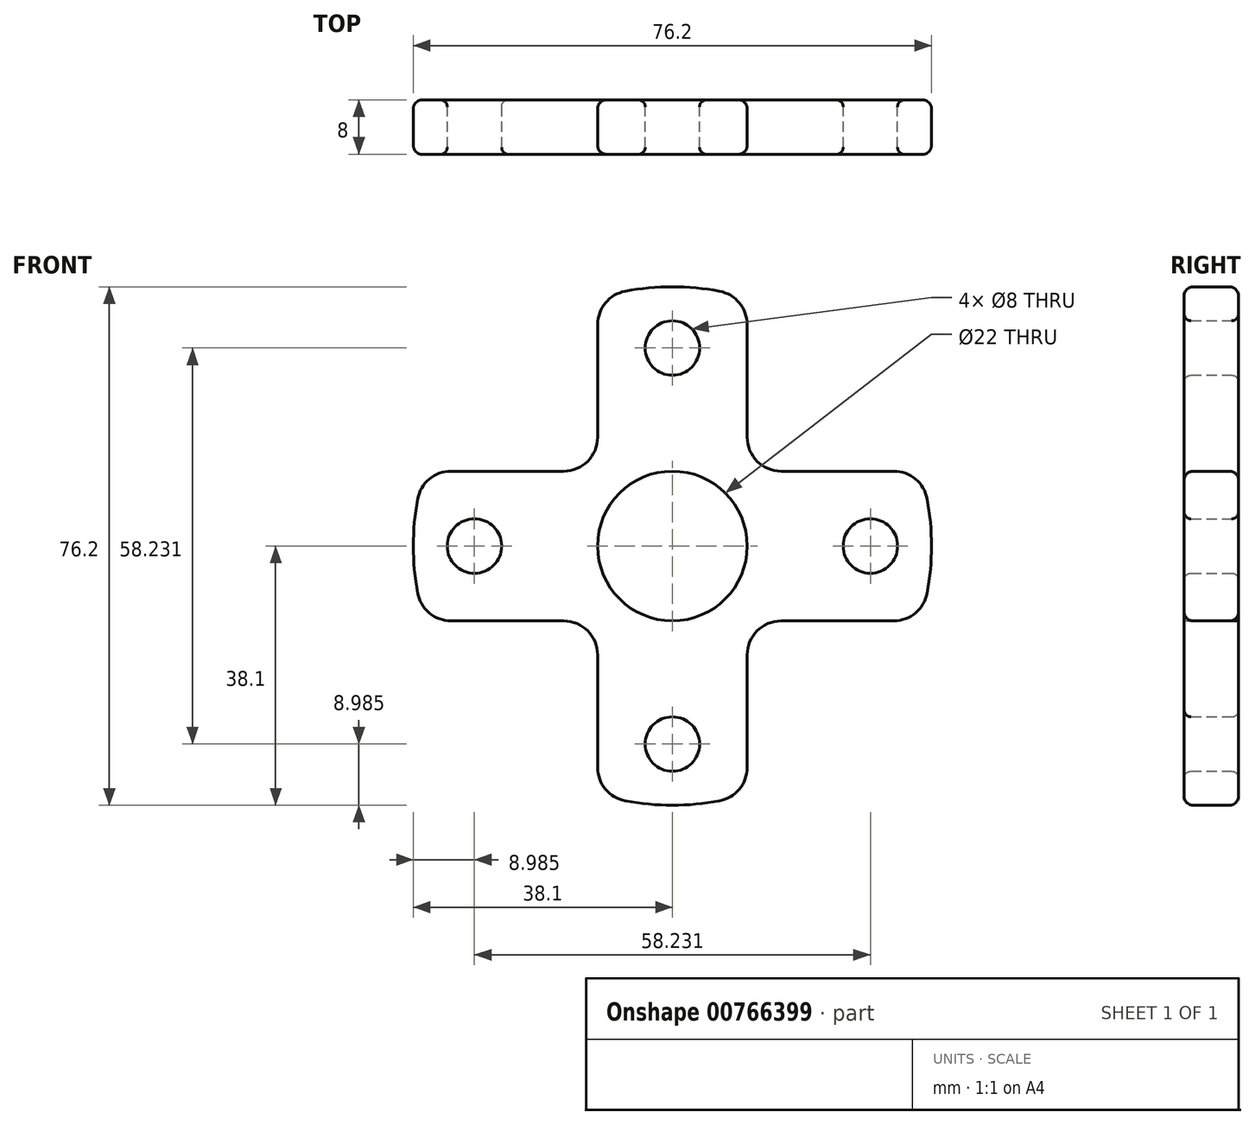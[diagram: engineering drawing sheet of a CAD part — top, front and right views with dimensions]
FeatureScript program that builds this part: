
annotation { "Feature Type Name" : "Feature", "Feature Type Description" : "" }
export const myFeature = defineFeature(function(context is Context, id is Id, definition is map)
    precondition{}
    {
        {
            var Q0;
            Q0=qCreatedBy(makeId("Front.planeOp"),FACE);
            var sketch = newSketch(context, id + "F0", { "sketchPlane" : qUnion([Q0])});
            skArc(sketch, "E0", {"start": v(-37.47, 6.9) * mm, "mid": v(-38.1, 0) * mm, "end": v(-37.47, -6.9) * mm});
            skCircle(sketch, "E1", {"center": v(0, 0) * mm, "radius": 11 * mm});
            skLineSegment(sketch, "E2", {"start": v(16, 11) * mm, "end": v(32.55, 11) * mm});
            skLineSegment(sketch, "E3", {"start": v(16, -11) * mm, "end": v(32.55, -11) * mm});
            skLineSegment(sketch, "E4", {"start": v(-16, -11) * mm, "end": v(-32.55, -11) * mm});
            skLineSegment(sketch, "E5", {"start": v(-16, 11) * mm, "end": v(-32.55, 11) * mm});
            skLineSegment(sketch, "E6", {"start": v(11, -16) * mm, "end": v(11, -32.55) * mm});
            skLineSegment(sketch, "E7", {"start": v(-11, -16) * mm, "end": v(-11, -32.55) * mm});
            skLineSegment(sketch, "E8", {"start": v(11, 16) * mm, "end": v(11, 32.55) * mm});
            skLineSegment(sketch, "E9", {"start": v(-11, 16) * mm, "end": v(-11, 32.55) * mm});
            skPoint(sketch, "E10.orphan", {"position": v(0, 11) * mm});
            skPoint(sketch, "E11.orphan", {"position": v(11, 0) * mm});
            skPoint(sketch, "E12.orphan", {"position": v(-11, 0) * mm});
            skPoint(sketch, "E13.orphan", {"position": v(0, -11) * mm});
            skArc(sketch, "E14.trimOffspring", {"start": v(6.9, 37.47) * mm, "mid": v(0, 38.1) * mm, "end": v(-6.9, 37.47) * mm});
            skArc(sketch, "E15.trimOffspring", {"start": v(37.47, -6.9) * mm, "mid": v(38.1, 0) * mm, "end": v(37.47, 6.9) * mm});
            skArc(sketch, "E16.trimOffspring", {"start": v(-6.9, -37.47) * mm, "mid": v(0, -38.1) * mm, "end": v(6.9, -37.47) * mm});
            skPoint(sketch, "E17.visualSharp", {"position": v(11, 11) * mm});
            skArc(sketch, "E17.filletArc", {"start": v(11, 16) * mm, "mid": v(12.46, 12.46) * mm, "end": v(16, 11) * mm});
            skPoint(sketch, "E18.visualSharp", {"position": v(-11, 11) * mm});
            skArc(sketch, "E18.filletArc", {"start": v(-16, 11) * mm, "mid": v(-12.46, 12.46) * mm, "end": v(-11, 16) * mm});
            skPoint(sketch, "E19.visualSharp", {"position": v(11, -11) * mm});
            skArc(sketch, "E19.filletArc", {"start": v(16, -11) * mm, "mid": v(12.46, -12.46) * mm, "end": v(11, -16) * mm});
            skPoint(sketch, "E20.visualSharp", {"position": v(-11, -11) * mm});
            skArc(sketch, "E20.filletArc", {"start": v(-11, -16) * mm, "mid": v(-12.46, -12.46) * mm, "end": v(-16, -11) * mm});
            skPoint(sketch, "E21.visualSharp", {"position": v(-11, -36.48) * mm});
            skArc(sketch, "E21.filletArc", {"start": v(-11, -32.55) * mm, "mid": v(-9.84, -35.75) * mm, "end": v(-6.9, -37.47) * mm});
            skPoint(sketch, "E22.visualSharp", {"position": v(11, -36.48) * mm});
            skArc(sketch, "E22.filletArc", {"start": v(6.9, -37.47) * mm, "mid": v(9.84, -35.75) * mm, "end": v(11, -32.55) * mm});
            skPoint(sketch, "E23.visualSharp", {"position": v(36.48, -11) * mm});
            skArc(sketch, "E23.filletArc", {"start": v(32.55, -11) * mm, "mid": v(35.75, -9.84) * mm, "end": v(37.47, -6.9) * mm});
            skPoint(sketch, "E24.visualSharp", {"position": v(36.48, 11) * mm});
            skArc(sketch, "E24.filletArc", {"start": v(37.47, 6.9) * mm, "mid": v(35.75, 9.84) * mm, "end": v(32.55, 11) * mm});
            skPoint(sketch, "E25.visualSharp", {"position": v(11, 36.48) * mm});
            skArc(sketch, "E25.filletArc", {"start": v(11, 32.55) * mm, "mid": v(9.84, 35.75) * mm, "end": v(6.9, 37.47) * mm});
            skPoint(sketch, "E26.visualSharp", {"position": v(-11, 36.48) * mm});
            skArc(sketch, "E26.filletArc", {"start": v(-6.9, 37.47) * mm, "mid": v(-9.84, 35.75) * mm, "end": v(-11, 32.55) * mm});
            skPoint(sketch, "E27.visualSharp", {"position": v(-36.48, 11) * mm});
            skArc(sketch, "E27.filletArc", {"start": v(-32.55, 11) * mm, "mid": v(-35.75, 9.84) * mm, "end": v(-37.47, 6.9) * mm});
            skPoint(sketch, "E28.visualSharp", {"position": v(-36.48, -11) * mm});
            skArc(sketch, "E28.filletArc", {"start": v(-37.47, -6.9) * mm, "mid": v(-35.75, -9.84) * mm, "end": v(-32.55, -11) * mm});
            skCircle(sketch, "E29", {"center": v(0, 29.12) * mm, "radius": 4 * mm});
            skCircle(sketch, "E30.1.0", {"center": v(-29.12, 0) * mm, "radius": 4 * mm});
            skCircle(sketch, "E30.2.0", {"center": v(0, -29.12) * mm, "radius": 4 * mm});
            skCircle(sketch, "E30.3.0", {"center": v(29.12, 0) * mm, "radius": 4 * mm});
            skSolve(sketch);
        }
        {
            var Q0;
            Q0=makeQuery(id+"F0.imprint","IMPRINT",FACE,{"disambiguationData":[TD([[makeQuery(id+"F0.imprint","IMPRINT",EDGE,{"derivedFrom":sQuery(id+"F0.wireOp",EDGE,"E0")}),1.0]])]});
            extrude(context, id + "F1", {"entities" : qUnion([Q0]), "depth" : 8 * mm, "offsetDistance" : 25 * mm});
        }
        {
            var Q0;
            Q0=makeQuery(id+"F1.opExtrude","CAP_EDGE",EDGE,{"disambiguationData":[OSD([sQuery(id+"F0.wireOp",EDGE,"E6")])],"isStart":false});
            var Q1;
            Q1=makeQuery(id+"F1.opExtrude","CAP_EDGE",EDGE,{"disambiguationData":[OSD([sQuery(id+"F0.wireOp",EDGE,"E19.filletArc")])],"isStart":false});
            var Q2;
            Q2=makeQuery(id+"F1.opExtrude","CAP_EDGE",EDGE,{"disambiguationData":[OSD([sQuery(id+"F0.wireOp",EDGE,"E6")])],"isStart":true});
            fillet(context, id + "F2", {"entities" : qUnion([Q0, Q1, Q2]), "radius" : 1.3 * mm, "tangentPropagation" : true, "allowEdgeOverflow" : false});
        }
        {
            var Q0;
            Q0=makeQuery(id+"F1.opExtrude","CAP_EDGE",EDGE,{"disambiguationData":[OSD([sQuery(id+"F0.wireOp",EDGE,"E29")])],"isStart":false});
            var Q1;
            Q1=makeQuery(id+"F1.opExtrude","CAP_EDGE",EDGE,{"disambiguationData":[OSD([sQuery(id+"F0.wireOp",EDGE,"E30.1.0")])],"isStart":false});
            var Q2;
            Q2=makeQuery(id+"F1.opExtrude","CAP_EDGE",EDGE,{"disambiguationData":[OSD([sQuery(id+"F0.wireOp",EDGE,"E30.2.0")])],"isStart":false});
            var Q3;
            Q3=makeQuery(id+"F1.opExtrude","CAP_EDGE",EDGE,{"disambiguationData":[OSD([sQuery(id+"F0.wireOp",EDGE,"E30.3.0")])],"isStart":false});
            var Q4;
            Q4=makeQuery(id+"F1.opExtrude","CAP_EDGE",EDGE,{"disambiguationData":[OSD([sQuery(id+"F0.wireOp",EDGE,"E30.2.0")])],"isStart":true});
            var Q5;
            Q5=makeQuery(id+"F1.opExtrude","CAP_EDGE",EDGE,{"disambiguationData":[OSD([sQuery(id+"F0.wireOp",EDGE,"E30.3.0")])],"isStart":true});
            var Q6;
            Q6=makeQuery(id+"F1.opExtrude","CAP_EDGE",EDGE,{"disambiguationData":[OSD([sQuery(id+"F0.wireOp",EDGE,"E29")])],"isStart":true});
            var Q7;
            Q7=makeQuery(id+"F1.opExtrude","CAP_EDGE",EDGE,{"disambiguationData":[OSD([sQuery(id+"F0.wireOp",EDGE,"E30.1.0")])],"isStart":true});
            fillet(context, id + "F3", {"entities" : qUnion([Q0, Q1, Q2, Q3, Q4, Q5, Q6, Q7]), "radius" : 1 * mm, "tangentPropagation" : true, "allowEdgeOverflow" : false});
        }
    });
